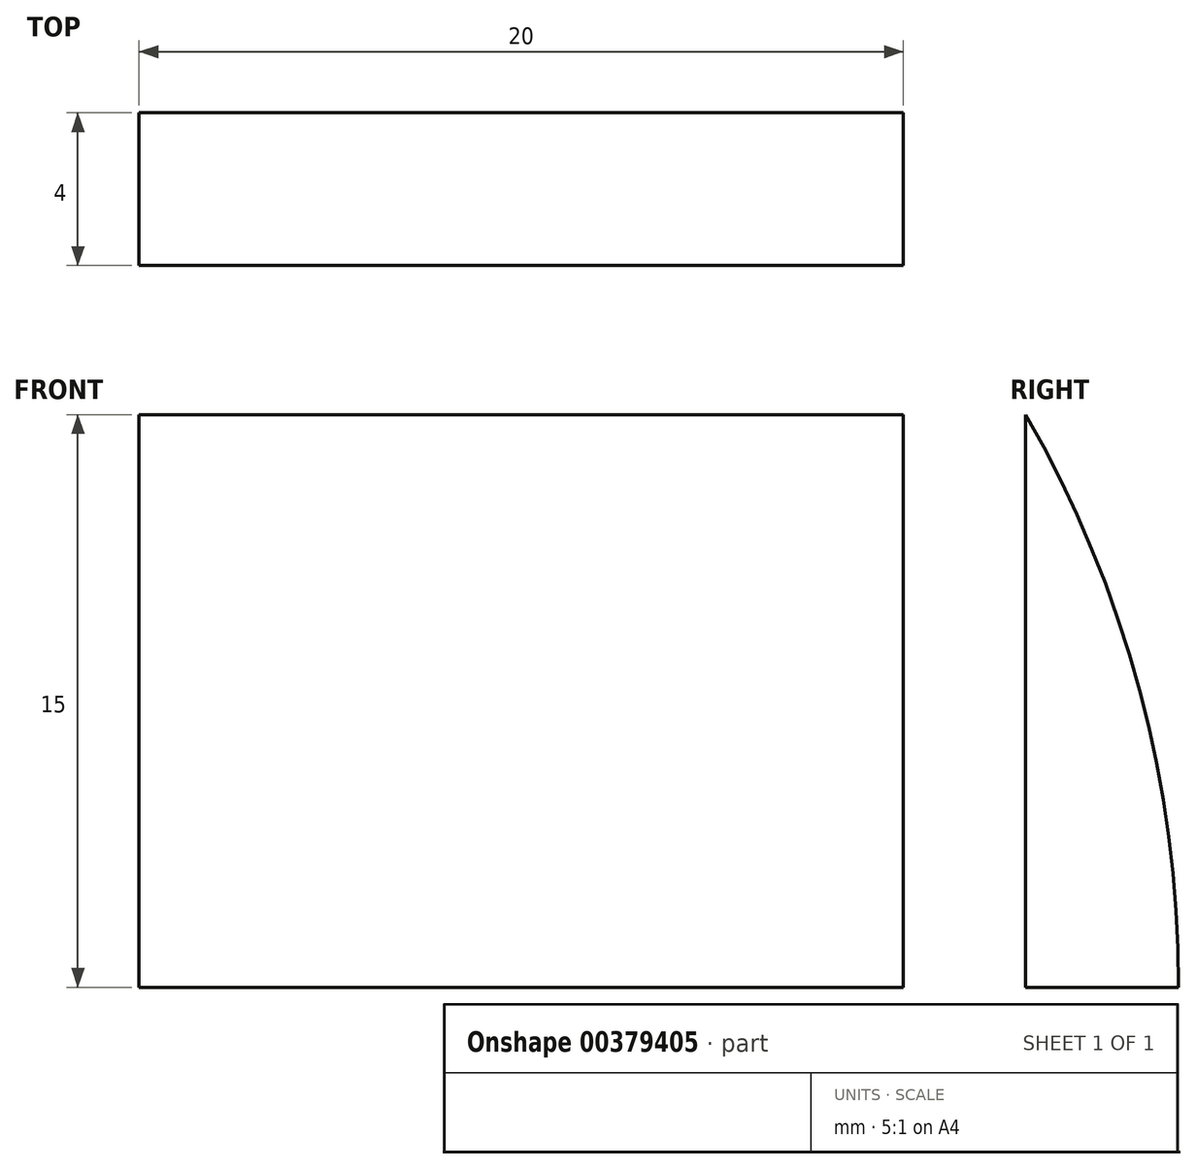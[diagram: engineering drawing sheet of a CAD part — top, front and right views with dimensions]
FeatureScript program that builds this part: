
annotation { "Feature Type Name" : "Feature", "Feature Type Description" : "" }
export const myFeature = defineFeature(function(context is Context, id is Id, definition is map)
    precondition{}
    {
        {
            var Q0;
            Q0=qCreatedBy(makeId("Front.planeOp"),FACE);
            var sketch = newSketch(context, id + "F0", { "sketchPlane" : qUnion([Q0])});
            skLineSegment(sketch, "E0.bottom", {"start": v(0, 0) * mm, "end": v(20, 0) * mm});
            skLineSegment(sketch, "E0.top", {"start": v(0, 15) * mm, "end": v(20, 15) * mm});
            skLineSegment(sketch, "E0.left", {"start": v(0, 0) * mm, "end": v(0, 15) * mm});
            skLineSegment(sketch, "E0.right", {"start": v(20, 0) * mm, "end": v(20, 15) * mm});
            skSolve(sketch);
        }
        {
            var Q0;
            Q0=makeQuery(id+"F0.imprint","IMPRINT",FACE,{"disambiguationData":[TD([[makeQuery(id+"F0.imprint","IMPRINT",EDGE,{"derivedFrom":sQuery(id+"F0.wireOp",EDGE,"E0.bottom")}),1.0]])]});
            extrude(context, id + "F1", {"entities" : qUnion([Q0]), "depth" : 4 * mm});
        }
        {
            var Q0;
            Q0=makeQuery(id+"F1.opExtrude","CAP_EDGE",EDGE,{"disambiguationData":[OSD([sQuery(id+"F0.wireOp",EDGE,"E0.top")])],"isStart":true});
            fillet(context, id + "F2", {"entities" : qUnion([Q0]), "radius" : 30 * mm, "tangentPropagation" : true, "allowEdgeOverflow" : false});
        }
    });
